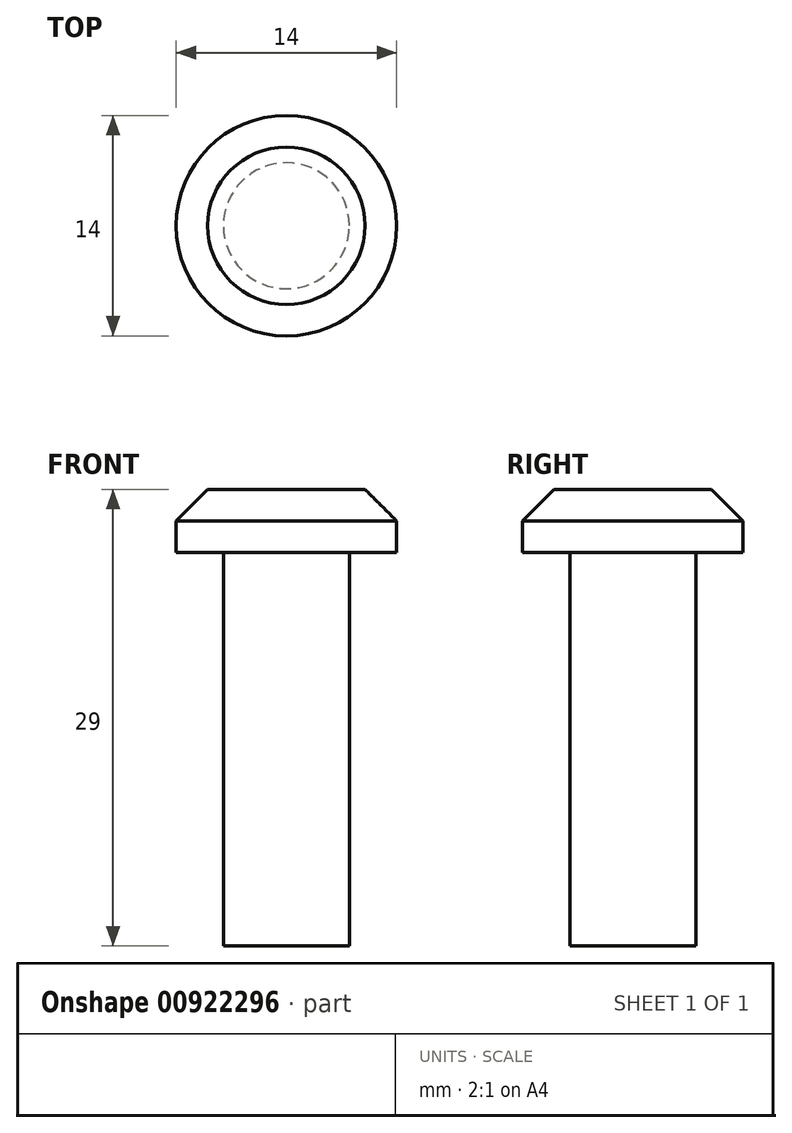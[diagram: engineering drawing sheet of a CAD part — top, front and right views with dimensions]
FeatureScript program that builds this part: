
annotation { "Feature Type Name" : "Feature", "Feature Type Description" : "" }
export const myFeature = defineFeature(function(context is Context, id is Id, definition is map)
    precondition{}
    {
        {
            var Q0;
            Q0=qCreatedBy(makeId("Front.planeOp"),FACE);
            var sketch = newSketch(context, id + "F0", { "sketchPlane" : qUnion([Q0])});
            skLineSegment(sketch, "E0", {"start": v(0, 0) * mm, "end": v(0, 35) * mm, "construction": true});
            skLineSegment(sketch, "E1", {"start": v(0, 0) * mm, "end": v(4, 0) * mm});
            skLineSegment(sketch, "E2", {"start": v(4, 0) * mm, "end": v(4, 25) * mm});
            skLineSegment(sketch, "E3", {"start": v(4, 25) * mm, "end": v(7, 25) * mm});
            skLineSegment(sketch, "E4", {"start": v(7, 25) * mm, "end": v(7, 29) * mm});
            skLineSegment(sketch, "E5", {"start": v(7, 29) * mm, "end": v(0, 29) * mm});
            skLineSegment(sketch, "E6", {"start": v(0, 29) * mm, "end": v(0, 0) * mm});
            skSolve(sketch);
        }
        {
            var Q0;
            Q0=makeQuery(id+"F0.imprint","IMPRINT",FACE,{"disambiguationData":[TD([[makeQuery(id+"F0.imprint","IMPRINT",EDGE,{"derivedFrom":sQuery(id+"F0.wireOp",EDGE,"E1")}),1.0]])]});
            var Q1;
            Q1=sQuery(id+"F0.wireOp",EDGE,"E0");
            revolve(context, id + "F1", {"surfaceOperationType" : NewSurfaceOperationType.NEW, "entities" : qUnion([Q0]), "axis" : qUnion([Q1]), "revolveType" : RevolveType.FULL});
        }
        {
            var Q0;
            Q0=makeQuery(id+"F1.opRevolve","SWEPT_EDGE",EDGE,{"disambiguationData":[OSD([sQuery(id+"F0.wireOp",EDGE,"E4"),sQuery(id+"F0.wireOp",EDGE,"E5")])]});
            chamfer(context, id + "F2", {"entities" : qUnion([Q0]), "width" : 2 * mm, "tangentPropagation" : true});
        }
    });
